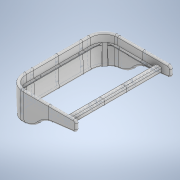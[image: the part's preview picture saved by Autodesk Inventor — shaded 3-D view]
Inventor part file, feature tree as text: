
AUTODESK INVENTOR PART (.ipt)
format: ipt  version: 2021 (Build 250183000, 183)  size: 2,812,928 bytes
history: native  units: mm
features: other x33, sketch x25, hole x19, projected_geometry x16, plane x13, extrude x9, fillet x7, mirror x4, loft x1, chamfer x1
ambient origin geometry x8: Origin, YZ Plane, XZ Plane, XY Plane, X Axis, Y Axis, Z Axis, Center Point
bodies: Body1 (feature_tree), Body2 (feature_tree), Body3 (feature_tree), Body4 (feature_tree), Body5 (feature_tree), Body6 (feature_tree), Body7 (feature_tree), Body8 (feature_tree), Body9 (feature_tree), Body10 (feature_tree), Body11 (feature_tree), Body12 (feature_tree), Body13 (feature_tree)
feature tree (128):
  sketch  "草圖1"
  plane  "工作平面1"
  sketch  "草圖2"
  plane  "工作平面2"
  sketch  "草圖3"
  sketch  "草圖5"
  plane  "工作平面4"
  loft  "斷面混成3"
  plane  "工作平面3"
  extrude  "擠出2"  Depth=700.0mm
  fillet  "圓角8"  Radius=500.0mm
  fillet  "圓角9"  Radius=20.0mm
  fillet  "圓角10"  Radius=20.0mm
  plane  "工作平面5"
  chamfer  "倒角2"  Distance=100.0mm
  hole  "孔1"  [1 undecoded]
  extrude  "擠出3"  [1 undecoded]
  hole  "孔2"  [1 undecoded]
  extrude  "擠出4"  [1 undecoded]
  fillet  "圓角12"  [1 undecoded]
  extrude  "擠出6"  [1 undecoded]
  mirror  "鏡射1"
  hole  "孔3"  [1 undecoded]
  extrude  "擠出7"  TaperAngle=0.0deg  [1 undecoded]
  hole  "孔4"  [1 undecoded]
  fillet  "圓角13"  Radius=75.0mm
  mirror  "鏡射2"
  extrude  "擠出8"  Depth=10.0mm
  mirror  "鏡射3"
  sketch  "草圖24"
  extrude  "擠出15"  Depth=325.0mm
  hole  "孔5"  [1 undecoded]
  mirror  "鏡射4"
  extrude  "擠出18"  Depth=150.0mm
  fillet  "圓角18"  Radius=20.0mm
  extrude  "擠出17"  [1 undecoded]
  fillet  "圓角17"  Radius=20.0mm
  plane  "工作平面6"
  plane  "工作平面7"
  other  "分割1"
  other  "分割2"
  plane  "工作平面9"
  plane  "工作平面11"
  plane  "工作平面13"
  other  "分割3"
  other  "分割4"
  other  "分割5"
  other  "分割6"
  other  "分割7"
  other  "分割8"
  other  "分割9"
  sketch  "草圖28"
  hole  "孔6"  [1 undecoded]
  hole  "孔7"  [1 undecoded]
  sketch  "草圖29"
  hole  "孔8"  [1 undecoded]
  hole  "孔9"  [1 undecoded]
  sketch  "草圖30"
  hole  "孔10"  [1 undecoded]
  hole  "孔11"  [1 undecoded]
  sketch  "草圖31"
  hole  "孔12"  [1 undecoded]
  hole  "孔13"  [1 undecoded]
  sketch  "草圖32"
  hole  "孔14"  [1 undecoded]
  sketch  "草圖33"
  hole  "孔15"  [1 undecoded]
  hole  "孔16"  [1 undecoded]
  hole  "孔17"  [1 undecoded]
  sketch  "草圖34"
  hole  "孔18"  [1 undecoded]
  hole  "孔19"  [1 undecoded]
  sketch  "草圖6"
  other  "實體3"
  sketch  "草圖7"
  sketch  "草圖8"
  sketch  "草圖9"
  projected_geometry  "投影迴路1"
  sketch  "草圖10"
  projected_geometry  "投影迴路2"
  other  "實體4"
  sketch  "草圖11"
  projected_geometry  "投影迴路3"
  projected_geometry  "投影迴路4"
  projected_geometry  "投影迴路5"
  projected_geometry  "投影迴路6"
  projected_geometry  "投影迴路7"
  projected_geometry  "投影迴路8"
  sketch  "草圖12"
  other  "實體5"
  projected_geometry  "投影迴路10"
  sketch  "草圖15"
  sketch  "草圖16"
  sketch  "草圖17"
  sketch  "草圖18"
  projected_geometry  "投影迴路11"
  sketch  "草圖26"
  projected_geometry  "投影迴路17"
  sketch  "草圖27"
  projected_geometry  "投影迴路18"
  other  "實體7"
  plane  "工作平面8"
  plane  "工作平面10"
  plane  "工作平面12"
  projected_geometry  "投影迴路19"
  projected_geometry  "投影迴路20"
  projected_geometry  "投影迴路21"
  projected_geometry  "投影迴路22"
  other  "投影切割邊1"
  other  "投影切割邊2"
  other  "實體8"
  other  "實體9"
  other  "實體10"
  other  "實體11"
  other  "實體12"
  other  "實體13"
  other  "實體14"
  other  "實體15"
  other  "實體16"
  other  "實體17"
  other  "實體18"
  other  "實體19"
  other  "實體20"
  other  "實體21"
  other  "實體22"
  other  "實體23"
  other  "實體24"
  other  "實體25"
note: 25 required parameter values undecoded (feature->parameter linkage not recoverable at this tier; creation-order binding heuristic only, values carry confidence <= 0.55)
